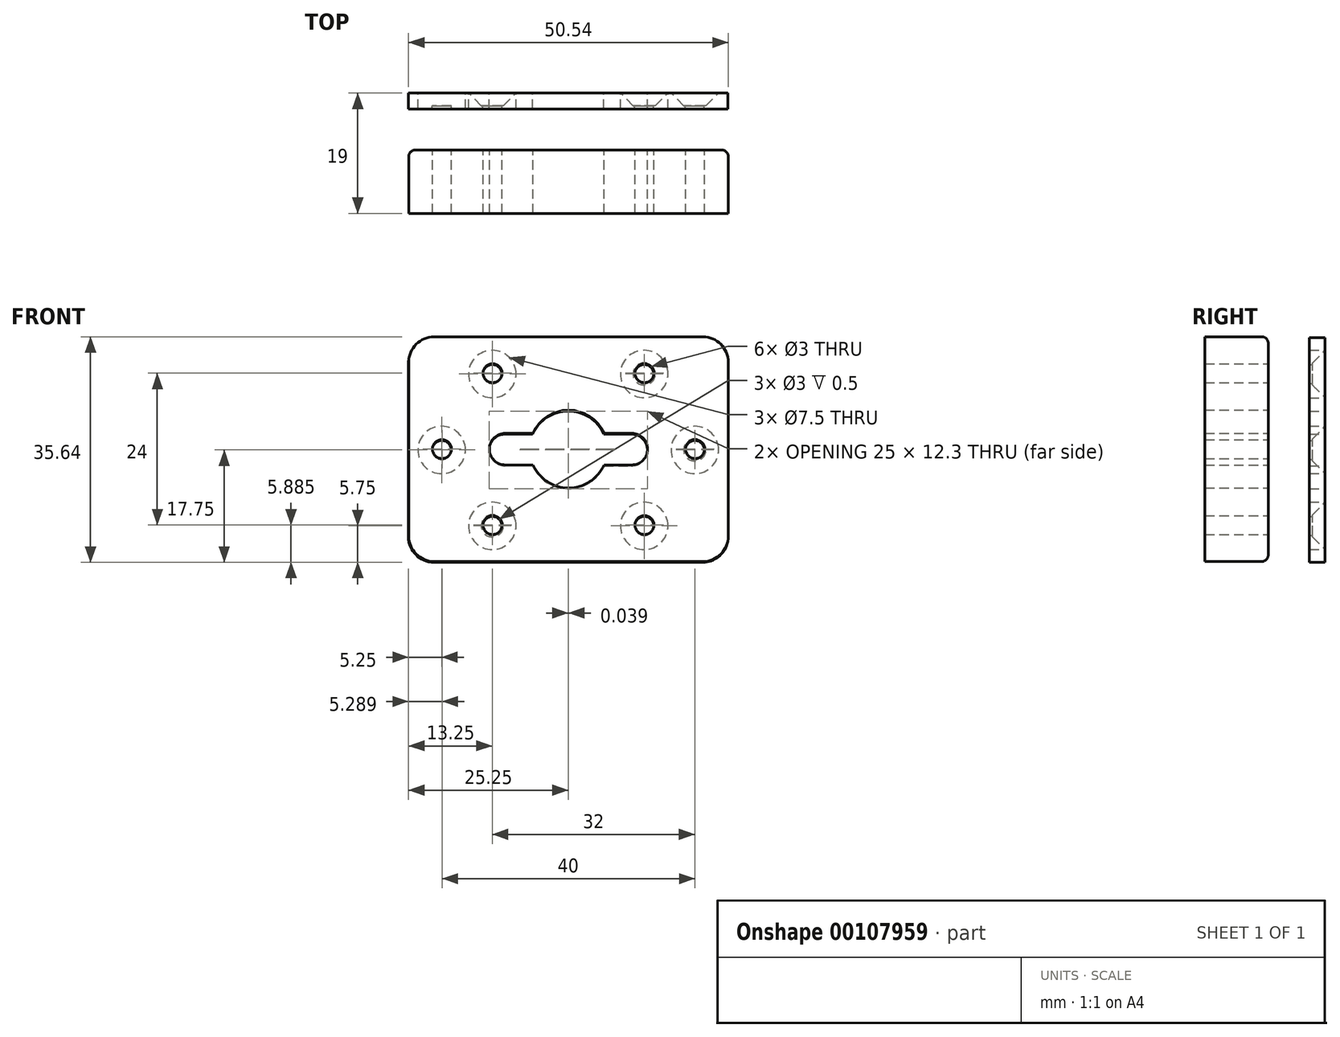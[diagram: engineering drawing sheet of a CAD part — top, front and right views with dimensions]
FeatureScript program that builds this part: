
annotation { "Feature Type Name" : "Feature", "Feature Type Description" : "" }
export const myFeature = defineFeature(function(context is Context, id is Id, definition is map)
    precondition{}
    {
        {
            var Q0;
            Q0=qCreatedBy(makeId("Front.planeOp"),FACE);
            var sketch = newSketch(context, id + "F0", { "sketchPlane" : qUnion([Q0])});
            skLineSegment(sketch, "E0.bottom", {"start": v(21.25, 17.75) * mm, "end": v(-21.25, 17.75) * mm});
            skLineSegment(sketch, "E0.top", {"start": v(21.25, -17.75) * mm, "end": v(-21.25, -17.75) * mm});
            skLineSegment(sketch, "E0.left", {"start": v(25.25, 13.75) * mm, "end": v(25.25, -13.75) * mm});
            skLineSegment(sketch, "E0.right", {"start": v(-25.25, 13.75) * mm, "end": v(-25.25, -13.75) * mm});
            skPoint(sketch, "E0.middle", {"position": v(0, 0) * mm});
            skPoint(sketch, "E1.visualSharp", {"position": v(-25.25, 17.75) * mm});
            skArc(sketch, "E1.filletArc", {"start": v(-21.25, 17.75) * mm, "mid": v(-24.08, 16.58) * mm, "end": v(-25.25, 13.75) * mm});
            skPoint(sketch, "E2.visualSharp", {"position": v(25.25, 17.75) * mm});
            skArc(sketch, "E2.filletArc", {"start": v(25.25, 13.75) * mm, "mid": v(24.08, 16.58) * mm, "end": v(21.25, 17.75) * mm});
            skPoint(sketch, "E3.visualSharp", {"position": v(25.25, -17.75) * mm});
            skArc(sketch, "E3.filletArc", {"start": v(21.25, -17.75) * mm, "mid": v(24.08, -16.58) * mm, "end": v(25.25, -13.75) * mm});
            skPoint(sketch, "E4.visualSharp", {"position": v(-25.25, -17.75) * mm});
            skArc(sketch, "E4.filletArc", {"start": v(-25.25, -13.75) * mm, "mid": v(-24.08, -16.58) * mm, "end": v(-21.25, -17.75) * mm});
            skCircle(sketch, "E5", {"center": v(0, 0) * mm, "radius": 6.15 * mm});
            skCircle(sketch, "E6", {"center": v(20, 0) * mm, "radius": 1.5 * mm});
            skCircle(sketch, "E7", {"center": v(12, 12) * mm, "radius": 1.5 * mm});
            skLineSegment(sketch, "E8", {"start": v(0, 17.75) * mm, "end": v(0, -17.75) * mm, "construction": true});
            skLineSegment(sketch, "E9", {"start": v(25.25, 0) * mm, "end": v(-25.25, 0) * mm, "construction": true});
            skCircle(sketch, "E10.MirrorC", {"center": v(12, -12) * mm, "radius": 1.5 * mm});
            skCircle(sketch, "E11.MirrorC", {"center": v(-12, 12) * mm, "radius": 1.5 * mm});
            skCircle(sketch, "E12.MirrorC", {"center": v(-20, 0) * mm, "radius": 1.5 * mm});
            skCircle(sketch, "E13.MirrorC", {"center": v(-12, -12) * mm, "radius": 1.5 * mm});
            skCircle(sketch, "E14", {"center": v(12, 12) * mm, "radius": 3.75 * mm});
            skCircle(sketch, "E15", {"center": v(20, 0) * mm, "radius": 3.75 * mm});
            skCircle(sketch, "E16", {"center": v(12, -12) * mm, "radius": 3.75 * mm});
            skCircle(sketch, "E17", {"center": v(-12, 12) * mm, "radius": 3.75 * mm});
            skCircle(sketch, "E18", {"center": v(-20, 0) * mm, "radius": 3.75 * mm});
            skCircle(sketch, "E19", {"center": v(-12, -12) * mm, "radius": 3.75 * mm});
            skCircle(sketch, "E20", {"center": v(-10, 0) * mm, "radius": 2.5 * mm});
            skLineSegment(sketch, "E21", {"start": v(0, 2.5) * mm, "end": v(-10, 2.5) * mm});
            skLineSegment(sketch, "E22.MirrorCS", {"start": v(0, -2.5) * mm, "end": v(-10, -2.5) * mm});
            skLineSegment(sketch, "E23.MirrorCS", {"start": v(0, 2.5) * mm, "end": v(10, 2.5) * mm});
            skLineSegment(sketch, "E24.MirrorCS", {"start": v(0, -2.5) * mm, "end": v(10, -2.5) * mm});
            skCircle(sketch, "E25.MirrorC", {"center": v(10, 0) * mm, "radius": 2.5 * mm});
            skSolve(sketch);
        }
        {
            var Q0;
            Q0=qCreatedBy(makeId("Front.planeOp"),FACE);
            cPlane(context, id + "F1", {"entities" : qUnion([Q0]), "cplaneType" : CPlaneType.OFFSET, "offset" : 9 * mm, "width" : 150 * mm, "height" : 150 * mm});
        }
        {
            var Q0;
            Q0=qCreatedBy(id+"F1.planeOp",FACE);
            var sketch = newSketch(context, id + "F2", { "sketchPlane" : qUnion([Q0])});
            skLineSegment(sketch, "E26.bottom", {"start": v(21.29, 17.89) * mm, "end": v(-21.21, 17.89) * mm});
            skLineSegment(sketch, "E26.top", {"start": v(21.29, -17.61) * mm, "end": v(-21.21, -17.61) * mm});
            skLineSegment(sketch, "E26.left", {"start": v(25.29, 13.89) * mm, "end": v(25.29, -13.61) * mm});
            skLineSegment(sketch, "E26.right", {"start": v(-25.21, 13.89) * mm, "end": v(-25.21, -13.61) * mm});
            skPoint(sketch, "E26.middle", {"position": v(0.04, 0.14) * mm});
            skPoint(sketch, "E27.visualSharp", {"position": v(-25.21, 17.89) * mm});
            skArc(sketch, "E27.filletArc", {"start": v(-21.21, 17.89) * mm, "mid": v(-24.04, 16.71) * mm, "end": v(-25.21, 13.89) * mm});
            skPoint(sketch, "E28.visualSharp", {"position": v(25.29, 17.89) * mm});
            skArc(sketch, "E28.filletArc", {"start": v(25.29, 13.89) * mm, "mid": v(24.12, 16.71) * mm, "end": v(21.29, 17.89) * mm});
            skPoint(sketch, "E29.visualSharp", {"position": v(25.29, -17.61) * mm});
            skArc(sketch, "E29.filletArc", {"start": v(21.29, -17.61) * mm, "mid": v(24.12, -16.44) * mm, "end": v(25.29, -13.61) * mm});
            skPoint(sketch, "E30.visualSharp", {"position": v(-25.21, -17.61) * mm});
            skArc(sketch, "E30.filletArc", {"start": v(-25.21, -13.61) * mm, "mid": v(-24.04, -16.44) * mm, "end": v(-21.21, -17.61) * mm});
            skCircle(sketch, "E31", {"center": v(0.04, 0.14) * mm, "radius": 6.15 * mm});
            skCircle(sketch, "E32", {"center": v(20.04, 0.14) * mm, "radius": 1.5 * mm});
            skCircle(sketch, "E33", {"center": v(12.04, 12.14) * mm, "radius": 1.5 * mm});
            skLineSegment(sketch, "E34", {"start": v(0.04, 17.89) * mm, "end": v(0.04, -17.61) * mm, "construction": true});
            skLineSegment(sketch, "E35", {"start": v(25.29, 0.14) * mm, "end": v(-25.21, 0.14) * mm, "construction": true});
            skCircle(sketch, "E36.MirrorC", {"center": v(12.04, -11.86) * mm, "radius": 1.5 * mm});
            skCircle(sketch, "E37.MirrorC", {"center": v(-11.96, 12.14) * mm, "radius": 1.5 * mm});
            skCircle(sketch, "E38.MirrorC", {"center": v(-19.96, 0.14) * mm, "radius": 1.5 * mm});
            skCircle(sketch, "E39.MirrorC", {"center": v(-11.96, -11.86) * mm, "radius": 1.5 * mm});
            skCircle(sketch, "E40", {"center": v(-9.96, 0.14) * mm, "radius": 2.5 * mm});
            skLineSegment(sketch, "E41", {"start": v(0.04, 2.64) * mm, "end": v(-9.96, 2.64) * mm});
            skLineSegment(sketch, "E42.MirrorCS", {"start": v(0.04, -2.36) * mm, "end": v(-9.96, -2.36) * mm});
            skLineSegment(sketch, "E43.MirrorCS", {"start": v(0.04, 2.64) * mm, "end": v(10.04, 2.64) * mm});
            skLineSegment(sketch, "E44.MirrorCS", {"start": v(0.04, -2.36) * mm, "end": v(10.04, -2.36) * mm});
            skCircle(sketch, "E45.MirrorC", {"center": v(10.04, 0.14) * mm, "radius": 2.5 * mm});
            skSolve(sketch);
        }
        {
            var Q0;
            Q0=makeQuery(id+"F0.imprint","IMPRINT",FACE,{"disambiguationData":[TD([[makeQuery(id+"F0.imprint","IMPRINT",EDGE,{"derivedFrom":sQuery(id+"F0.wireOp",EDGE,"E0.bottom")}),1.0]])]});
            var Q1;
            Q1=makeQuery(id+"F0.imprint","IMPRINT",FACE,{"disambiguationData":[TD([[makeQuery(id+"F0.imprint","IMPRINT",EDGE,{"derivedFrom":sQuery(id+"F0.wireOp",EDGE,"E11.MirrorC")}),1.0]])]});
            var Q2;
            Q2=makeQuery(id+"F0.imprint","IMPRINT",FACE,{"disambiguationData":[TD([[makeQuery(id+"F0.imprint","IMPRINT",EDGE,{"derivedFrom":sQuery(id+"F0.wireOp",EDGE,"E12.MirrorC")}),1.0]])]});
            var Q3;
            Q3=makeQuery(id+"F0.imprint","IMPRINT",FACE,{"disambiguationData":[TD([[makeQuery(id+"F0.imprint","IMPRINT",EDGE,{"derivedFrom":sQuery(id+"F0.wireOp",EDGE,"E13.MirrorC")}),-1.0]])]});
            var Q4;
            Q4=makeQuery(id+"F0.imprint","IMPRINT",FACE,{"disambiguationData":[TD([[makeQuery(id+"F0.imprint","IMPRINT",EDGE,{"derivedFrom":sQuery(id+"F0.wireOp",EDGE,"E10.MirrorC")}),1.0]])]});
            var Q5;
            Q5=makeQuery(id+"F0.imprint","IMPRINT",FACE,{"disambiguationData":[TD([[makeQuery(id+"F0.imprint","IMPRINT",EDGE,{"derivedFrom":sQuery(id+"F0.wireOp",EDGE,"E6")}),-1.0]])]});
            var Q6;
            Q6=makeQuery(id+"F0.imprint","IMPRINT",FACE,{"disambiguationData":[TD([[makeQuery(id+"F0.imprint","IMPRINT",EDGE,{"derivedFrom":sQuery(id+"F0.wireOp",EDGE,"E7")}),-1.0]])]});
            extrude(context, id + "F3", {"entities" : qUnion([Q0, Q1, Q2, Q3, Q4, Q5, Q6]), "depth" : 2.5 * mm});
        }
        {
            var Q0;
            Q0=makeQuery(id+"F0.imprint","IMPRINT",FACE,{"disambiguationData":[TD([[makeQuery(id+"F0.imprint","IMPRINT",EDGE,{"derivedFrom":sQuery(id+"F0.wireOp",EDGE,"E12.MirrorC")}),1.0]])]});
            var Q1;
            Q1=makeQuery(id+"F0.imprint","IMPRINT",FACE,{"disambiguationData":[TD([[makeQuery(id+"F0.imprint","IMPRINT",EDGE,{"derivedFrom":sQuery(id+"F0.wireOp",EDGE,"E10.MirrorC")}),1.0]])]});
            var Q2;
            Q2=makeQuery(id+"F0.imprint","IMPRINT",FACE,{"disambiguationData":[TD([[makeQuery(id+"F0.imprint","IMPRINT",EDGE,{"derivedFrom":sQuery(id+"F0.wireOp",EDGE,"E11.MirrorC")}),1.0]])]});
            var Q3;
            Q3=makeQuery(id+"F0.imprint","IMPRINT",FACE,{"disambiguationData":[TD([[makeQuery(id+"F0.imprint","IMPRINT",EDGE,{"derivedFrom":sQuery(id+"F0.wireOp",EDGE,"E7")}),-1.0]])]});
            var Q4;
            Q4=makeQuery(id+"F0.imprint","IMPRINT",FACE,{"disambiguationData":[TD([[makeQuery(id+"F0.imprint","IMPRINT",EDGE,{"derivedFrom":sQuery(id+"F0.wireOp",EDGE,"E13.MirrorC")}),-1.0]])]});
            var Q5;
            Q5=makeQuery(id+"F0.imprint","IMPRINT",FACE,{"disambiguationData":[TD([[makeQuery(id+"F0.imprint","IMPRINT",EDGE,{"derivedFrom":sQuery(id+"F0.wireOp",EDGE,"E6")}),-1.0]])]});
            var Q6;
            Q6=makeQuery(id+"F0.imprint","IMPRINT",FACE,{"disambiguationData":[TD([[makeQuery(id+"F0.imprint","IMPRINT",EDGE,{"derivedFrom":sQuery(id+"F0.wireOp",EDGE,"E11.MirrorC")}),-1.0]])]});
            var Q7;
            Q7=makeQuery(id+"F0.imprint","IMPRINT",FACE,{"disambiguationData":[TD([[makeQuery(id+"F0.imprint","IMPRINT",EDGE,{"derivedFrom":sQuery(id+"F0.wireOp",EDGE,"E12.MirrorC")}),-1.0]])]});
            var Q8;
            Q8=makeQuery(id+"F0.imprint","IMPRINT",FACE,{"disambiguationData":[TD([[makeQuery(id+"F0.imprint","IMPRINT",EDGE,{"derivedFrom":sQuery(id+"F0.wireOp",EDGE,"E13.MirrorC")}),1.0]])]});
            var Q9;
            Q9=makeQuery(id+"F0.imprint","IMPRINT",FACE,{"disambiguationData":[TD([[makeQuery(id+"F0.imprint","IMPRINT",EDGE,{"derivedFrom":sQuery(id+"F0.wireOp",EDGE,"E10.MirrorC")}),-1.0]])]});
            var Q10;
            Q10=makeQuery(id+"F0.imprint","IMPRINT",FACE,{"disambiguationData":[TD([[makeQuery(id+"F0.imprint","IMPRINT",EDGE,{"derivedFrom":sQuery(id+"F0.wireOp",EDGE,"E6")}),1.0]])]});
            var Q11;
            Q11=makeQuery(id+"F0.imprint","IMPRINT",FACE,{"disambiguationData":[TD([[makeQuery(id+"F0.imprint","IMPRINT",EDGE,{"derivedFrom":sQuery(id+"F0.wireOp",EDGE,"E7")}),1.0]])]});
            extrude(context, id + "F4", {"entities" : qUnion([Q0, Q1, Q2, Q3, Q4, Q5, Q6, Q7, Q8, Q9, Q10, Q11]), "operationType" : NewBodyOperationType.REMOVE, "depth" : 2 * mm, "hasDraft" : true, "draftAngle" : 45 * degree, "draftPullDirection" : true});
        }
        {
            var Q0;
            Q0 = qSketchRegion(id + "F2", true);
            extrude(context, id + "F5", {"entities" : qUnion([Q0]), "depth" : 10 * mm});
        }
        {
            var Q0;
            Q0=makeQuery(id+"F5.opExtrude","CAP_EDGE",EDGE,{"disambiguationData":[OSD([sQuery(id+"F2.wireOp",EDGE,"E26.left")])],"isStart":true});
            var Q1;
            Q1=makeQuery(id+"F5.opExtrude","CAP_EDGE",EDGE,{"disambiguationData":[OSD([sQuery(id+"F2.wireOp",EDGE,"E29.filletArc")])],"isStart":true});
            var Q2;
            Q2=makeQuery(id+"F5.opExtrude","CAP_EDGE",EDGE,{"disambiguationData":[OSD([sQuery(id+"F2.wireOp",EDGE,"E26.top")])],"isStart":true});
            var Q3;
            Q3=makeQuery(id+"F5.opExtrude","CAP_EDGE",EDGE,{"disambiguationData":[OSD([sQuery(id+"F2.wireOp",EDGE,"E28.filletArc")])],"isStart":true});
            var Q4;
            Q4=makeQuery(id+"F5.opExtrude","CAP_EDGE",EDGE,{"disambiguationData":[OSD([sQuery(id+"F2.wireOp",EDGE,"E30.filletArc")])],"isStart":true});
            var Q5;
            Q5=makeQuery(id+"F5.opExtrude","CAP_EDGE",EDGE,{"disambiguationData":[OSD([sQuery(id+"F2.wireOp",EDGE,"E26.right")])],"isStart":true});
            var Q6;
            Q6=makeQuery(id+"F5.opExtrude","CAP_EDGE",EDGE,{"disambiguationData":[OSD([sQuery(id+"F2.wireOp",EDGE,"E27.filletArc")])],"isStart":true});
            var Q7;
            Q7=makeQuery(id+"F5.opExtrude","CAP_EDGE",EDGE,{"disambiguationData":[OSD([sQuery(id+"F2.wireOp",EDGE,"E26.bottom")])],"isStart":true});
            fillet(context, id + "F6", {"entities" : qUnion([Q0, Q1, Q2, Q3, Q4, Q5, Q6, Q7]), "radius" : 1 * mm, "tangentPropagation" : true, "allowEdgeOverflow" : false});
        }
    });
